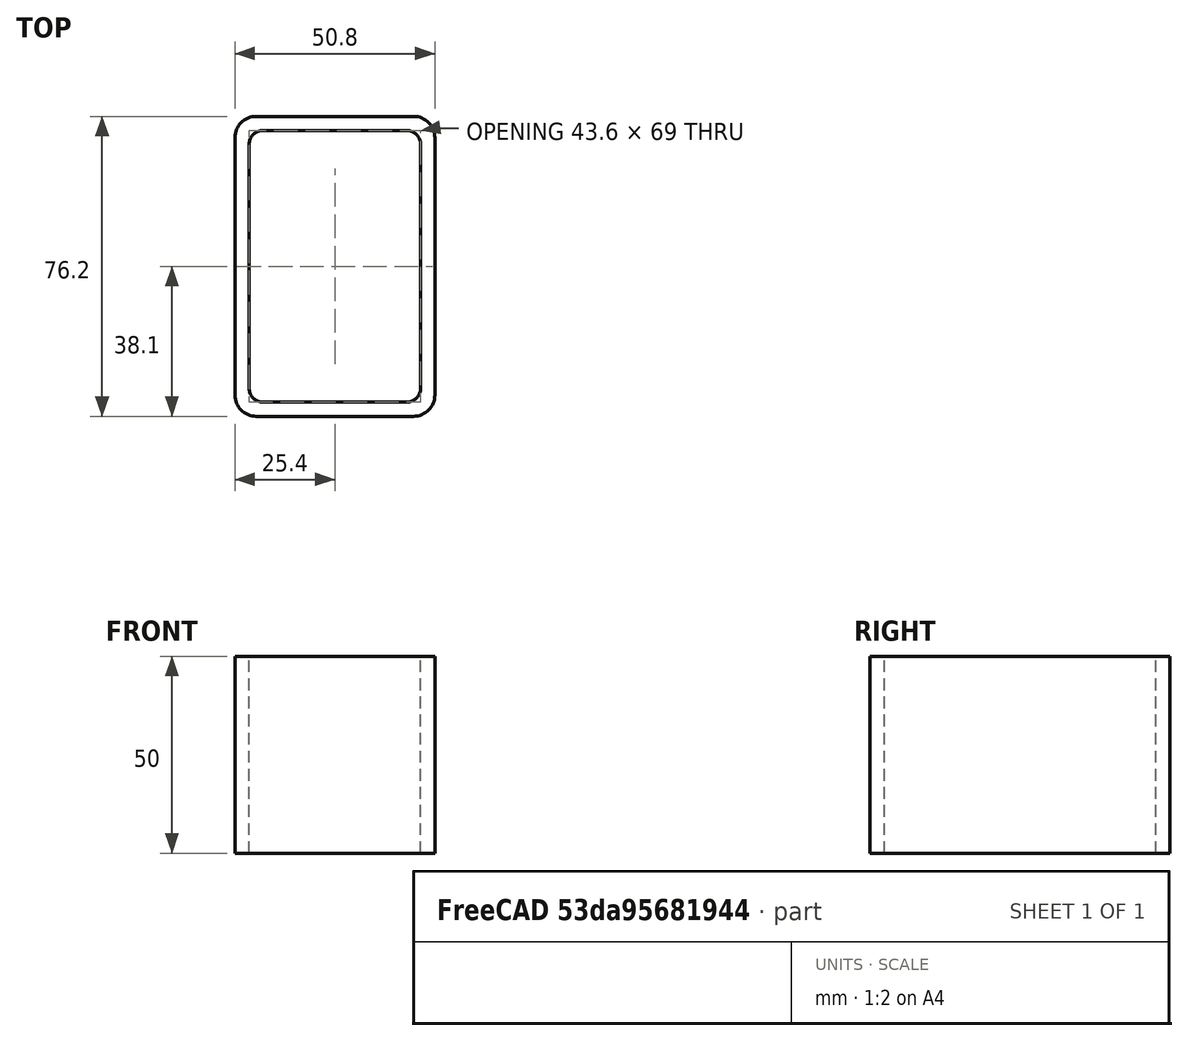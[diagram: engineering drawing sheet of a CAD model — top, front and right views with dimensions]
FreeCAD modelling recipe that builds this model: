
FCSTD DOCUMENT  (FreeCAD 0.15R4671 (Git))
Label: Rectangular hollow section 76.2 x50.8 x3.6 EN10219 S235JRH
License: All rights reserved
LicenseURL: http://en.wikipedia.org/wiki/All_rights_reserved
objects: Sketcher::SketchObject×1, Part::Extrusion×1
note: 2 computed .brp shape members not serialized (recipe doc carries the construction recipe); baked Part::Feature solids carry a one-line shape summary decoded from their .brp

FEATURE [Sketcher::SketchObject] Sketch
  sketch-geometry (16):
    g0: LineSegment StartX=-18.2 StartY=34.5 StartZ=0 EndX=18.2 EndY=34.5 EndZ=0
    g1: LineSegment StartX=21.8 StartY=30.9 StartZ=0 EndX=21.8 EndY=-30.9 EndZ=0
    g2: LineSegment StartX=18.2 StartY=-34.5 StartZ=0 EndX=-18.2 EndY=-34.5 EndZ=0
    g3: LineSegment StartX=-21.8 StartY=-30.9 StartZ=0 EndX=-21.8 EndY=30.9 EndZ=0
    g4: LineSegment StartX=-20 StartY=38.1 StartZ=0 EndX=20 EndY=38.1 EndZ=0
    g5: LineSegment StartX=25.4 StartY=32.7 StartZ=0 EndX=25.4 EndY=-32.7 EndZ=0
    g6: LineSegment StartX=20 StartY=-38.1 StartZ=0 EndX=-20 EndY=-38.1 EndZ=0
    g7: LineSegment StartX=-25.4 StartY=-32.7 StartZ=0 EndX=-25.4 EndY=32.7 EndZ=0
    g8: ArcOfCircle CenterX=-18.2 CenterY=30.9 CenterZ=0 NormalX=0 NormalY=0 NormalZ=1 Radius=3.6 StartAngle=1.5708 EndAngle=3.14159
    g9: ArcOfCircle CenterX=18.2 CenterY=30.9 CenterZ=0 NormalX=0 NormalY=0 NormalZ=1 Radius=3.6 StartAngle=0 EndAngle=1.5708
    g10: ArcOfCircle CenterX=18.2 CenterY=-30.9 CenterZ=0 NormalX=0 NormalY=0 NormalZ=1 Radius=3.6 StartAngle=4.71239 EndAngle=6.28319
    g11: ArcOfCircle CenterX=-18.2 CenterY=-30.9 CenterZ=0 NormalX=0 NormalY=0 NormalZ=1 Radius=3.6 StartAngle=3.14159 EndAngle=4.71239
    g12: ArcOfCircle CenterX=20 CenterY=32.7 CenterZ=0 NormalX=0 NormalY=0 NormalZ=1 Radius=5.4 StartAngle=0 EndAngle=1.5708
    g13: ArcOfCircle CenterX=20 CenterY=-32.7 CenterZ=0 NormalX=0 NormalY=0 NormalZ=1 Radius=5.4 StartAngle=4.71239 EndAngle=6.28319
    g14: ArcOfCircle CenterX=-20 CenterY=-32.7 CenterZ=0 NormalX=0 NormalY=0 NormalZ=1 Radius=5.4 StartAngle=3.14159 EndAngle=4.71239
    g15: ArcOfCircle CenterX=-20 CenterY=32.7 CenterZ=0 NormalX=0 NormalY=0 NormalZ=1 Radius=5.4 StartAngle=1.5708 EndAngle=3.14159
  constraints (36):
    c: Horizontal(g2)
    c: Vertical(g3)
    c: Horizontal(g6)
    c: Vertical(g7)
    c: Tangent(g3,g8) = 1.5708
    c: Tangent(g0,g8) = 1.5708
    c: Tangent(g0,g9) = 1.5708
    c: Tangent(g1,g9) = 1.5708
    c: Tangent(g1,g10) = 1.5708
    c: Tangent(g2,g10) = 1.5708
    c: Tangent(g2,g11) = 1.5708
    c: Tangent(g3,g11) = 1.5708
    c: Tangent(g4,g12) = 1.5708
    c: Tangent(g5,g12) = 1.5708
    c: Tangent(g5,g13) = 1.5708
    c: Tangent(g6,g13) = 1.5708
    c: Tangent(g6,g14) = 1.5708
    c: Tangent(g7,g14) = 1.5708
    c: Tangent(g7,g15) = 1.5708
    c: Tangent(g4,g15) = 1.5708
    c: Equal(g9,g8)
    c: Equal(g9,g11)
    c: Equal(g9,g10)
    c: Equal(g12,g15)
    c: Equal(g12,g14)
    c: Equal(g12,g13)
    c: Symmetric(g4,g6,g-1)
    c: Symmetric(g7,g5,g-2)
    c: DistanceY(g4,g6) = -76.2
    c: DistanceX(g7,g5) = 50.8
    c: Symmetric(g3,g1,g-2)
    c: Symmetric(g0,g2,g-1)
    c: DistanceY(g0,g4) = 3.6
    c: DistanceX(g5,g1) = -3.6
    c: Radius(g9) = 3.6
    c: Radius(g12) = 5.4
FEATURE [Part::Extrusion] Extrude  label="Rectangular hollow section 76.2 x50.8 x3.6 EN10219 S235JRH"
  Base = -> Sketch
  Dir = (0,0,50)
  Solid = true
